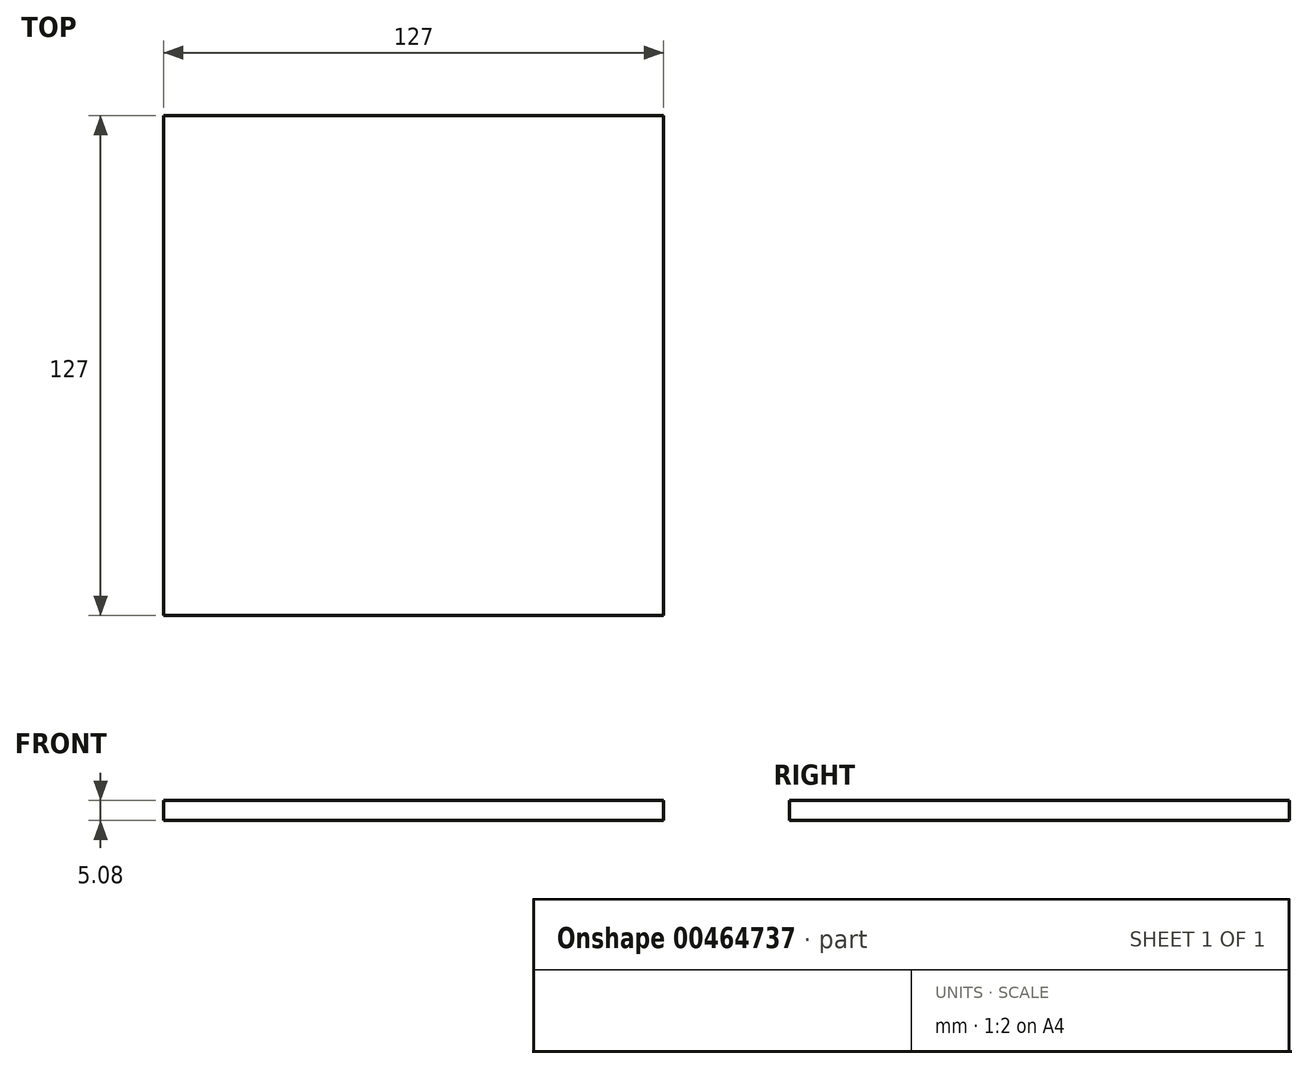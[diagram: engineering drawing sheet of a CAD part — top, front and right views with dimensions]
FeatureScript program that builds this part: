
annotation { "Feature Type Name" : "Feature", "Feature Type Description" : "" }
export const myFeature = defineFeature(function(context is Context, id is Id, definition is map)
    precondition{}
    {
        {
            var Q0;
            Q0=qCreatedBy(makeId("Top.planeOp"),FACE);
            var sketch = newSketch(context, id + "F0", { "sketchPlane" : qUnion([Q0])});
            skLineSegment(sketch, "E0.bottom", {"start": v(63.5, 63.5) * mm, "end": v(-63.5, 63.5) * mm});
            skLineSegment(sketch, "E0.top", {"start": v(63.5, -63.5) * mm, "end": v(-63.5, -63.5) * mm});
            skLineSegment(sketch, "E0.left", {"start": v(63.5, 63.5) * mm, "end": v(63.5, -63.5) * mm});
            skLineSegment(sketch, "E0.right", {"start": v(-63.5, 63.5) * mm, "end": v(-63.5, -63.5) * mm});
            skPoint(sketch, "E0.middle", {"position": v(0, 0) * mm});
            skSolve(sketch);
        }
        {
            var Q0;
            Q0=makeQuery(id+"F0.imprint","IMPRINT",FACE,{"disambiguationData":[TD([[makeQuery(id+"F0.imprint","IMPRINT",EDGE,{"derivedFrom":sQuery(id+"F0.wireOp",EDGE,"E0.bottom")}),1.0]])]});
            extrude(context, id + "F1", {"entities" : qUnion([Q0]), "depth" : 5.08 * mm});
        }
    });
